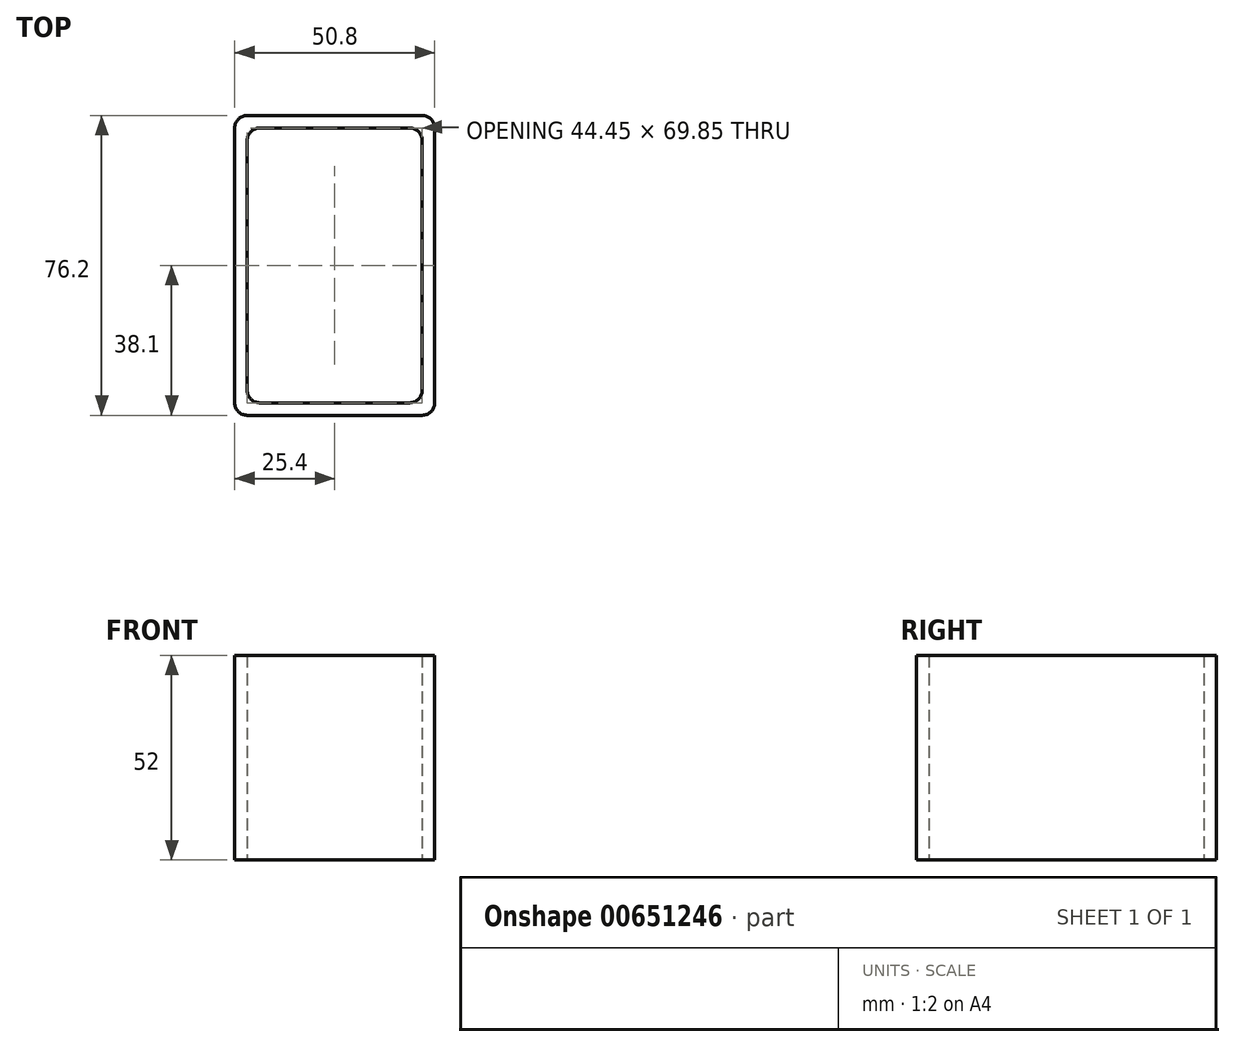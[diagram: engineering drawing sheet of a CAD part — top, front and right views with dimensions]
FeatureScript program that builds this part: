
annotation { "Feature Type Name" : "Feature", "Feature Type Description" : "" }
export const myFeature = defineFeature(function(context is Context, id is Id, definition is map)
    precondition{}
    {
        {
            var Q0;
            Q0=qCreatedBy(makeId("Top.planeOp"),FACE);
            var sketch = newSketch(context, id + "F0", { "sketchPlane" : qUnion([Q0])});
            skLineSegment(sketch, "E0.bottom", {"start": v(25.4, -38.1) * mm, "end": v(-25.4, -38.1) * mm});
            skLineSegment(sketch, "E0.top", {"start": v(25.4, 38.1) * mm, "end": v(-25.4, 38.1) * mm});
            skLineSegment(sketch, "E0.left", {"start": v(25.4, -38.1) * mm, "end": v(25.4, 38.1) * mm});
            skLineSegment(sketch, "E0.right", {"start": v(-25.4, -38.1) * mm, "end": v(-25.4, 38.1) * mm});
            skPoint(sketch, "E0.middle", {"position": v(0, 0) * mm});
            skLineSegment(sketch, "E1.bottom", {"start": v(22.23, -34.92) * mm, "end": v(-22.23, -34.92) * mm});
            skLineSegment(sketch, "E1.top", {"start": v(22.23, 34.93) * mm, "end": v(-22.22, 34.93) * mm});
            skLineSegment(sketch, "E1.left", {"start": v(22.23, -34.92) * mm, "end": v(22.23, 34.93) * mm});
            skLineSegment(sketch, "E1.right", {"start": v(-22.23, -34.92) * mm, "end": v(-22.22, 34.93) * mm});
            skSolve(sketch);
        }
        {
            assignVariable(context, id + "F1", {"name" : "Length", "anyValue" : 52});
        }
        {
            var Q0;
            Q0=makeQuery(id+"F0.imprint","IMPRINT",FACE,{"disambiguationData":[TD([[makeQuery(id+"F0.imprint","IMPRINT",EDGE,{"derivedFrom":sQuery(id+"F0.wireOp",EDGE,"E0.bottom")}),-1.0]])]});
            extrude(context, id + "F2", {"entities" : qUnion([Q0]), "depth" : (getVariable(context, 'Length')) * mm, "offsetDistance" : 25.4 * mm});
        }
        {
            var Q0;
            Q0=makeQuery(id+"F2.opExtrude","SWEPT_EDGE",EDGE,{"disambiguationData":[OSD([sQuery(id+"F0.wireOp",EDGE,"E0.top"),sQuery(id+"F0.wireOp",EDGE,"E0.left")])]});
            var Q1;
            Q1=makeQuery(id+"F2.opExtrude","SWEPT_EDGE",EDGE,{"disambiguationData":[OSD([sQuery(id+"F0.wireOp",EDGE,"E0.top"),sQuery(id+"F0.wireOp",EDGE,"E0.right")])]});
            var Q2;
            Q2=makeQuery(id+"F2.opExtrude","SWEPT_EDGE",EDGE,{"disambiguationData":[OSD([sQuery(id+"F0.wireOp",EDGE,"E0.bottom"),sQuery(id+"F0.wireOp",EDGE,"E0.left")])]});
            var Q3;
            Q3=makeQuery(id+"F2.opExtrude","SWEPT_EDGE",EDGE,{"disambiguationData":[OSD([sQuery(id+"F0.wireOp",EDGE,"E1.bottom"),sQuery(id+"F0.wireOp",EDGE,"E1.left")])]});
            var Q4;
            Q4=makeQuery(id+"F2.opExtrude","SWEPT_EDGE",EDGE,{"disambiguationData":[OSD([sQuery(id+"F0.wireOp",EDGE,"E1.bottom"),sQuery(id+"F0.wireOp",EDGE,"E1.right")])]});
            var Q5;
            Q5=makeQuery(id+"F2.opExtrude","SWEPT_EDGE",EDGE,{"disambiguationData":[OSD([sQuery(id+"F0.wireOp",EDGE,"E1.top"),sQuery(id+"F0.wireOp",EDGE,"E1.right")])]});
            var Q6;
            Q6=makeQuery(id+"F2.opExtrude","SWEPT_EDGE",EDGE,{"disambiguationData":[OSD([sQuery(id+"F0.wireOp",EDGE,"E1.top"),sQuery(id+"F0.wireOp",EDGE,"E1.left")])]});
            var Q7;
            Q7=makeQuery(id+"F2.opExtrude","SWEPT_EDGE",EDGE,{"disambiguationData":[OSD([sQuery(id+"F0.wireOp",EDGE,"E0.bottom"),sQuery(id+"F0.wireOp",EDGE,"E0.right")])]});
            fillet(context, id + "F3", {"entities" : qUnion([Q0, Q1, Q2, Q3, Q4, Q5, Q6, Q7]), "radius" : 3.17 * mm, "tangentPropagation" : true, "allowEdgeOverflow" : false});
        }
    });
